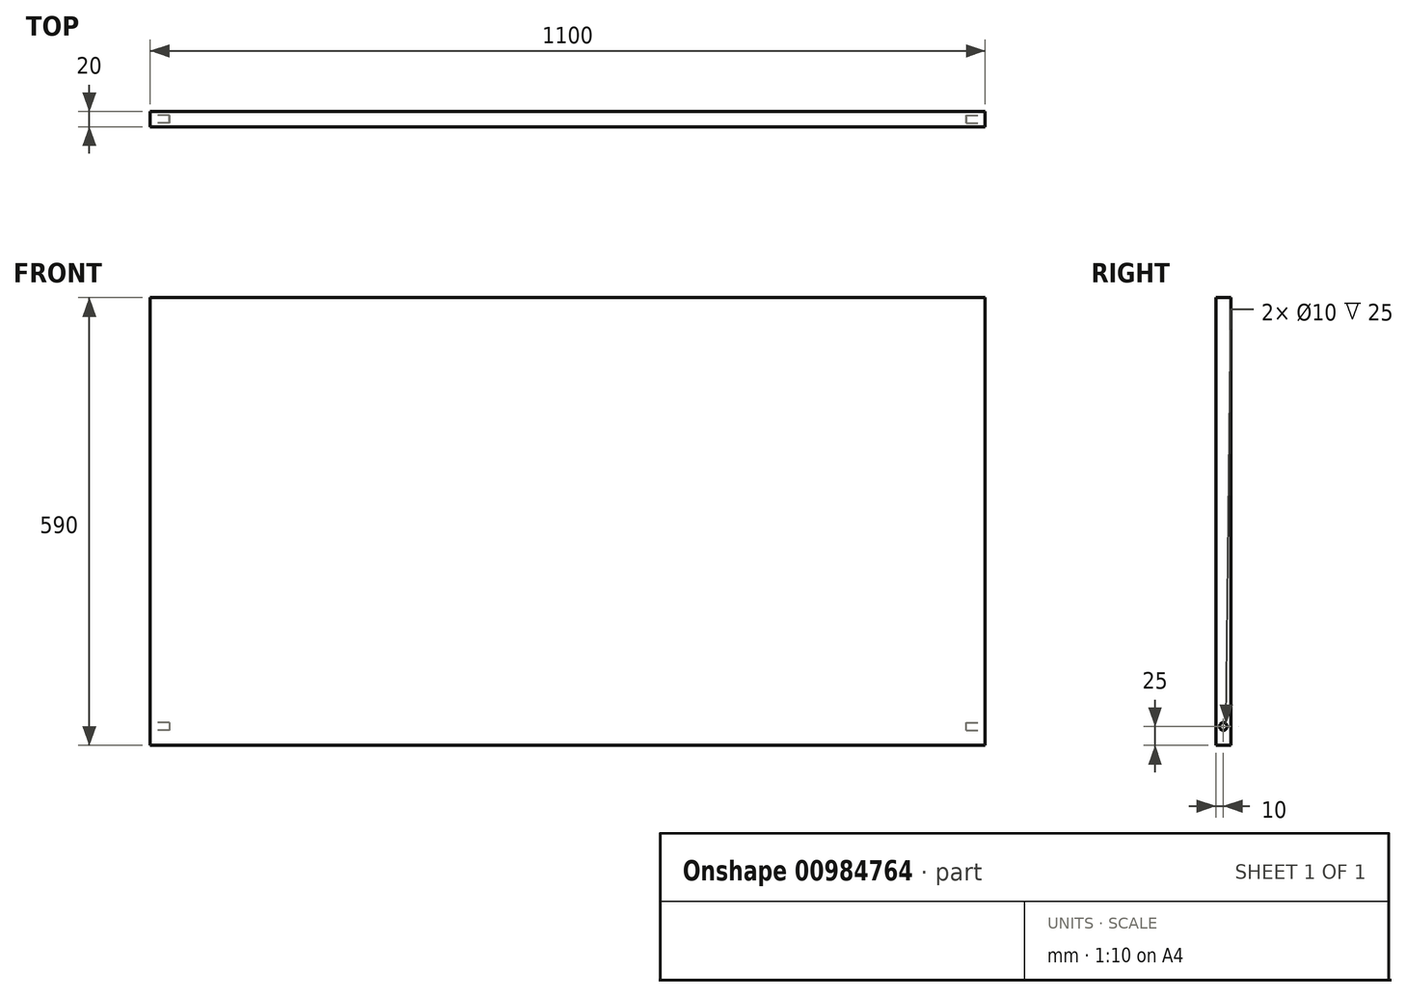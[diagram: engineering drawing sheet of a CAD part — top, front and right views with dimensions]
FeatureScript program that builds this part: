
annotation { "Feature Type Name" : "Feature", "Feature Type Description" : "" }
export const myFeature = defineFeature(function(context is Context, id is Id, definition is map)
    precondition{}
    {
        {
            var Q0;
            Q0=qCreatedBy(makeId("Front.planeOp"),FACE);
            var sketch = newSketch(context, id + "F0", { "sketchPlane" : qUnion([Q0])});
            skLineSegment(sketch, "E0.bottom", {"start": v(550, -295) * mm, "end": v(-550, -295) * mm});
            skLineSegment(sketch, "E0.top", {"start": v(550, 295) * mm, "end": v(-550, 295) * mm});
            skLineSegment(sketch, "E0.left", {"start": v(550, -295) * mm, "end": v(550, 295) * mm});
            skLineSegment(sketch, "E0.right", {"start": v(-550, -295) * mm, "end": v(-550, 295) * mm});
            skPoint(sketch, "E0.middle", {"position": v(0, 0) * mm});
            skSolve(sketch);
        }
        {
            var Q0;
            Q0 = qSketchRegion(id + "F0", true);
            extrude(context, id + "F1", {"entities" : qUnion([Q0]), "depth" : 20 * mm, "offsetDistance" : 25 * mm});
        }
        {
            var Q0;
            Q0=makeQuery(id+"F1.opExtrude","SWEPT_FACE",FACE,{"disambiguationData":[OSD([sQuery(id+"F0.wireOp",EDGE,"E0.left")])]});
            var sketch = newSketch(context, id + "F2", { "sketchPlane" : qUnion([Q0])});
            skCircle(sketch, "E1", {"center": v(-10, -270) * mm, "radius": 5 * mm});
            skSolve(sketch);
        }
        {
            var Q0;
            Q0 = qSketchRegion(id + "F2", true);
            extrude(context, id + "F3", {"entities" : qUnion([Q0]), "operationType" : NewBodyOperationType.REMOVE, "oppositeDirection" : true, "depth" : 25 * mm, "offsetDistance" : 25 * mm});
        }
        {
            var Q0;
            Q0=makeQuery(id+"F1.opExtrude","SWEPT_FACE",FACE,{"disambiguationData":[OSD([sQuery(id+"F0.wireOp",EDGE,"E0.right")])]});
            var sketch = newSketch(context, id + "F4", { "sketchPlane" : qUnion([Q0])});
            skCircle(sketch, "E2", {"center": v(10, -270) * mm, "radius": 5 * mm});
            skSolve(sketch);
        }
        {
            var Q0;
            Q0 = qSketchRegion(id + "F4", true);
            extrude(context, id + "F5", {"entities" : qUnion([Q0]), "operationType" : NewBodyOperationType.REMOVE, "oppositeDirection" : true, "depth" : 25 * mm, "offsetDistance" : 25 * mm});
        }
    });
